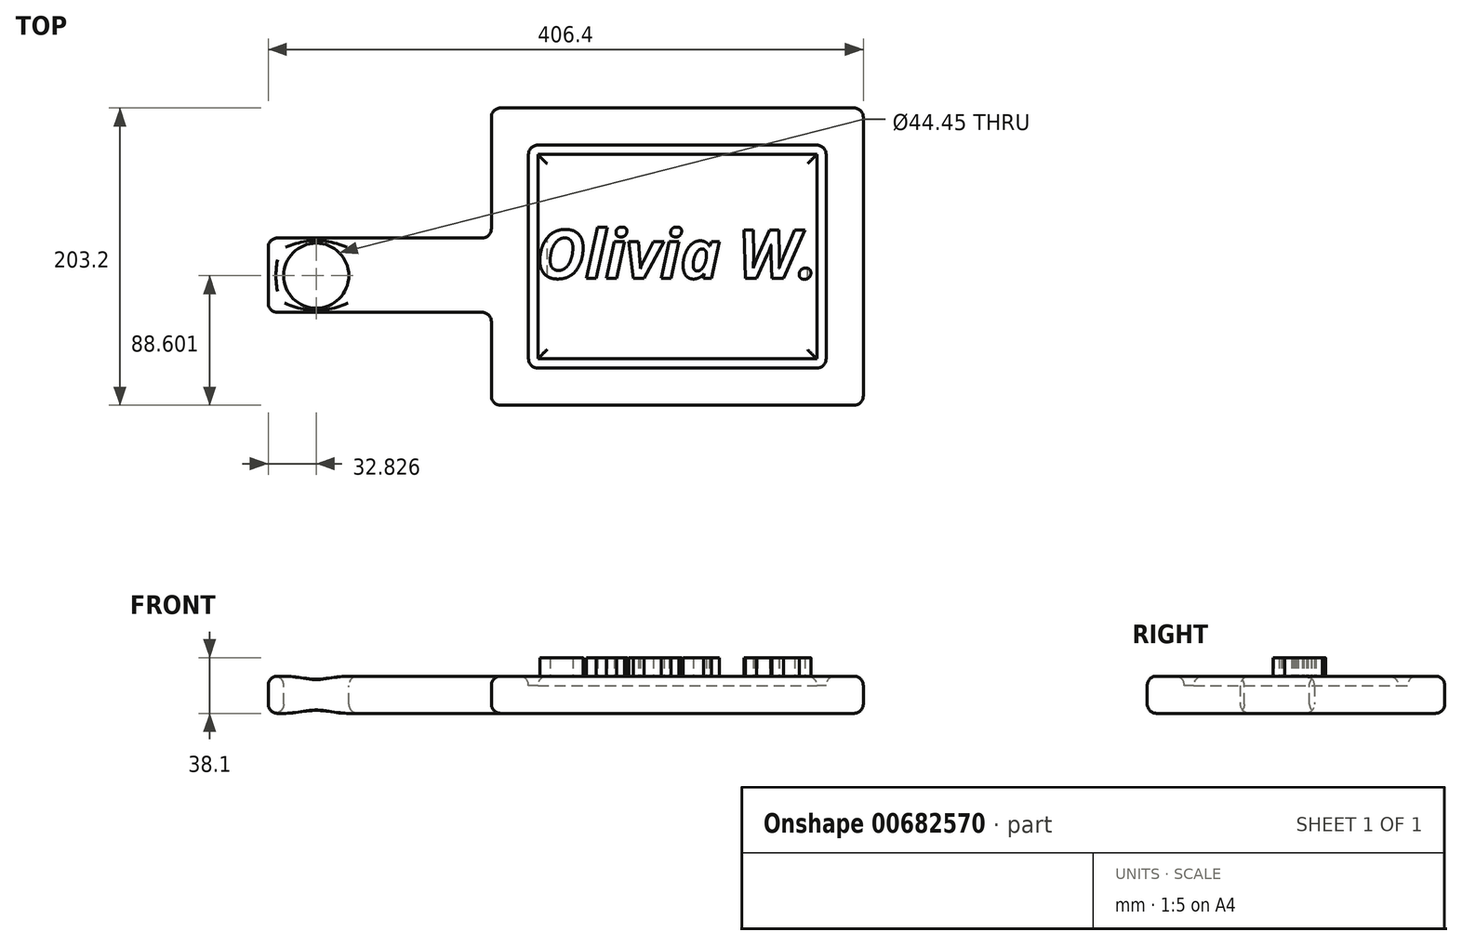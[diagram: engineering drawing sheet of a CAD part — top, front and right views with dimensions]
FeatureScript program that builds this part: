
annotation { "Feature Type Name" : "Feature", "Feature Type Description" : "" }
export const myFeature = defineFeature(function(context is Context, id is Id, definition is map)
    precondition{}
    {
        {
            var Q0;
            Q0=qCreatedBy(makeId("Top.planeOp"),FACE);
            var sketch = newSketch(context, id + "F0", { "sketchPlane" : qUnion([Q0])});
            skLineSegment(sketch, "E0.bottom", {"start": v(0, 0) * mm, "end": v(254, 0) * mm});
            skLineSegment(sketch, "E0.top", {"start": v(0, 203.2) * mm, "end": v(254, 203.2) * mm});
            skLineSegment(sketch, "E0.left", {"start": v(0, 0) * mm, "end": v(0, 203.2) * mm});
            skLineSegment(sketch, "E0.right", {"start": v(254, 0) * mm, "end": v(254, 203.2) * mm});
            skLineSegment(sketch, "E1.bottom", {"start": v(0, 114.3) * mm, "end": v(-152.4, 114.3) * mm});
            skLineSegment(sketch, "E1.top", {"start": v(0, 63.5) * mm, "end": v(-152.4, 63.5) * mm});
            skLineSegment(sketch, "E1.left", {"start": v(0, 114.3) * mm, "end": v(0, 63.5) * mm});
            skLineSegment(sketch, "E1.right", {"start": v(-152.4, 114.3) * mm, "end": v(-152.4, 63.5) * mm});
            skSolve(sketch);
        }
        {
            var Q0;
            {var subQ3=sQuery(id+"F0.wireOp",EDGE,"E0.bottom");Q0=makeQuery(id+"F0.imprint","IMPRINT",FACE,{"disambiguationData":[TD([[makeQuery(id+"F0.imprint","IMPRINT",EDGE,{"derivedFrom":subQ3}),1.0]])]});}
            var sketch = newSketch(context, id + "F1", { "sketchPlane" : qUnion([Q0])});
            skSolve(sketch);
        }
        {
            var Q0;
            Q0 = qSketchRegion(id + "F1", true);
            var Q1;
            {var subQ3=sQuery(id+"F0.wireOp",EDGE,"E0.bottom");Q1=makeQuery(id+"F0.imprint","IMPRINT",FACE,{"disambiguationData":[TD([[makeQuery(id+"F0.imprint","IMPRINT",EDGE,{"derivedFrom":subQ3}),1.0]])]});}
            var Q2;
            Q2=makeQuery(id+"F0.imprint","IMPRINT",FACE,{"disambiguationData":[TD([[makeQuery(id+"F0.imprint","IMPRINT",EDGE,{"derivedFrom":sQuery(id+"F0.wireOp",EDGE,"E1.bottom")}),1.0]])]});
            extrude(context, id + "F2", {"entities" : qUnion([Q0, Q1, Q2]), "depth" : 25.4 * mm, "offsetDistance" : 25.4 * mm});
        }
        {
            var Q0;
            Q0=makeQuery(id+"F2.opExtrude","CAP_FACE",FACE,{"disambiguationData":[OSD([sQuery(id+"F0.wireOp",EDGE,"E0.bottom"),sQuery(id+"F0.wireOp",EDGE,"E0.top"),sQuery(id+"F0.wireOp",EDGE,"E0.left"),sQuery(id+"F0.wireOp",EDGE,"E0.right"),sQuery(id+"F0.wireOp",EDGE,"E1.bottom"),sQuery(id+"F0.wireOp",EDGE,"E1.top"),sQuery(id+"F0.wireOp",EDGE,"E1.right")])],"isStart":false});
            var sketch = newSketch(context, id + "F3", { "sketchPlane" : qUnion([Q0])});
            skCircle(sketch, "E2", {"center": v(-119.57, 88.6) * mm, "radius": 22.23 * mm});
            skSolve(sketch);
        }
        {
            var Q0;
            Q0=makeQuery(id+"F3.imprint","IMPRINT",FACE,{"disambiguationData":[TD([[makeQuery(id+"F3.imprint","IMPRINT",EDGE,{"derivedFrom":sQuery(id+"F3.wireOp",EDGE,"E2")}),1.0]])]});
            extrude(context, id + "F4", {"entities" : qUnion([Q0]), "operationType" : NewBodyOperationType.REMOVE, "oppositeDirection" : true, "depth" : 25.4 * mm, "offsetDistance" : 25.4 * mm});
        }
        {
            var Q0;
            Q0=makeQuery(id+"F2.opExtrude","CAP_FACE",FACE,{"disambiguationData":[OSD([sQuery(id+"F0.wireOp",EDGE,"E0.bottom"),sQuery(id+"F0.wireOp",EDGE,"E0.top"),sQuery(id+"F0.wireOp",EDGE,"E0.left"),sQuery(id+"F0.wireOp",EDGE,"E0.right"),sQuery(id+"F0.wireOp",EDGE,"E1.bottom"),sQuery(id+"F0.wireOp",EDGE,"E1.top"),sQuery(id+"F0.wireOp",EDGE,"E1.right")])],"isStart":false});
            var sketch = newSketch(context, id + "F5", { "sketchPlane" : qUnion([Q0])});
            skLineSegment(sketch, "E3.0", {"start": v(0, 177.8) * mm, "end": v(254, 177.8) * mm});
            skLineSegment(sketch, "E4.0", {"start": v(25.4, 0) * mm, "end": v(25.4, 63.5) * mm});
            skLineSegment(sketch, "E5.0", {"start": v(25.4, 114.3) * mm, "end": v(25.4, 203.2) * mm});
            skLineSegment(sketch, "E6.0", {"start": v(0, 25.4) * mm, "end": v(254, 25.4) * mm});
            skLineSegment(sketch, "E7.0", {"start": v(228.6, 0) * mm, "end": v(228.6, 203.2) * mm});
            skLineSegment(sketch, "E8", {"start": v(25.4, 114.3) * mm, "end": v(25.4, 63.5) * mm});
            skLineSegment(sketch, "E9.0", {"start": v(0, 171.45) * mm, "end": v(254, 171.45) * mm});
            skLineSegment(sketch, "E10.0", {"start": v(31.75, 114.3) * mm, "end": v(31.75, 203.2) * mm});
            skLineSegment(sketch, "E10.1", {"start": v(31.75, 114.3) * mm, "end": v(31.75, 63.5) * mm});
            skLineSegment(sketch, "E10.2", {"start": v(31.75, 0) * mm, "end": v(31.75, 63.5) * mm});
            skLineSegment(sketch, "E11.0", {"start": v(0, 31.75) * mm, "end": v(254, 31.75) * mm});
            skLineSegment(sketch, "E12.0", {"start": v(222.25, 0) * mm, "end": v(222.25, 203.2) * mm});
            skSolve(sketch);
        }
        {
            var Q0;
            {var subQ0=sQuery(id+"F5.wireOp",EDGE,"E5.0");var subQ1=sQuery(id+"F5.wireOp",EDGE,"E3.0");var subQ2=makeQuery(id+"F5.imprint","INTERSECT",VERTEX,{"derivedFrom":[subQ1,subQ0]});Q0=makeQuery(id+"F5.imprint","IMPRINT",FACE,{"disambiguationData":[TD([[makeQuery(id+"F5.imprint","IMPRINT",EDGE,{"disambiguationData":[TD([[subQ2,-1.0]])],"derivedFrom":subQ1}),-1.0]])]});}
            var Q1;
            {var subQ0=sQuery(id+"F5.wireOp",EDGE,"E10.0");var subQ1=sQuery(id+"F5.wireOp",EDGE,"E3.0");var subQ2=makeQuery(id+"F5.imprint","INTERSECT",VERTEX,{"derivedFrom":[subQ1,subQ0]});Q1=makeQuery(id+"F5.imprint","IMPRINT",FACE,{"disambiguationData":[TD([[makeQuery(id+"F5.imprint","IMPRINT",EDGE,{"disambiguationData":[TD([[subQ2,-1.0]])],"derivedFrom":subQ1}),-1.0]])]});}
            var Q2;
            {var subQ0=sQuery(id+"F5.wireOp",EDGE,"E12.0");var subQ1=sQuery(id+"F5.wireOp",EDGE,"E3.0");var subQ2=makeQuery(id+"F5.imprint","INTERSECT",VERTEX,{"derivedFrom":[subQ1,subQ0]});Q2=makeQuery(id+"F5.imprint","IMPRINT",FACE,{"disambiguationData":[TD([[makeQuery(id+"F5.imprint","IMPRINT",EDGE,{"disambiguationData":[TD([[subQ2,-1.0]])],"derivedFrom":subQ1}),-1.0]])]});}
            var Q3;
            {var subQ0=sQuery(id+"F5.wireOp",EDGE,"E6.0");var subQ1=sQuery(id+"F5.wireOp",EDGE,"E4.0");var subQ2=makeQuery(id+"F5.imprint","INTERSECT",VERTEX,{"derivedFrom":[subQ1,subQ0]});Q3=makeQuery(id+"F5.imprint","IMPRINT",FACE,{"disambiguationData":[TD([[makeQuery(id+"F5.imprint","IMPRINT",EDGE,{"disambiguationData":[TD([[subQ2,-1.0]])],"derivedFrom":subQ1}),-1.0]])]});}
            var Q4;
            {var subQ0=sQuery(id+"F5.wireOp",EDGE,"E10.2");var subQ1=sQuery(id+"F5.wireOp",EDGE,"E6.0");var subQ2=makeQuery(id+"F5.imprint","INTERSECT",VERTEX,{"derivedFrom":[subQ1,subQ0]});Q4=makeQuery(id+"F5.imprint","IMPRINT",FACE,{"disambiguationData":[TD([[makeQuery(id+"F5.imprint","IMPRINT",EDGE,{"disambiguationData":[TD([[subQ2,-1.0]])],"derivedFrom":subQ1}),1.0]])]});}
            var Q5;
            {var subQ0=sQuery(id+"F5.wireOp",EDGE,"E12.0");var subQ1=sQuery(id+"F5.wireOp",EDGE,"E6.0");var subQ2=makeQuery(id+"F5.imprint","INTERSECT",VERTEX,{"derivedFrom":[subQ1,subQ0]});Q5=makeQuery(id+"F5.imprint","IMPRINT",FACE,{"disambiguationData":[TD([[makeQuery(id+"F5.imprint","IMPRINT",EDGE,{"disambiguationData":[TD([[subQ2,-1.0]])],"derivedFrom":subQ1}),1.0]])]});}
            var Q6;
            {var subQ0=sQuery(id+"F5.wireOp",EDGE,"E11.0");var subQ1=sQuery(id+"F5.wireOp",EDGE,"E7.0");var subQ2=makeQuery(id+"F5.imprint","INTERSECT",VERTEX,{"derivedFrom":[subQ1,subQ0]});Q6=makeQuery(id+"F5.imprint","IMPRINT",FACE,{"disambiguationData":[TD([[makeQuery(id+"F5.imprint","IMPRINT",EDGE,{"disambiguationData":[TD([[subQ2,-1.0]])],"derivedFrom":subQ1}),1.0]])]});}
            var Q7;
            {var subQ0=sQuery(id+"F5.wireOp",EDGE,"E8");Q7=makeQuery(id+"F5.imprint","IMPRINT",FACE,{"disambiguationData":[TD([[makeQuery(id+"F5.imprint","IMPRINT",EDGE,{"derivedFrom":subQ0}),1.0]])]});}
            extrude(context, id + "F6", {"entities" : qUnion([Q0, Q1, Q2, Q3, Q4, Q5, Q6, Q7]), "operationType" : NewBodyOperationType.REMOVE, "oppositeDirection" : true, "depth" : 6.35 * mm, "offsetDistance" : 25.4 * mm});
        }
        {
            var Q0;
            Q0=makeQuery(id+"F2.opExtrude","SWEPT_EDGE",EDGE,{"disambiguationData":[OSD([sQuery(id+"F0.wireOp",EDGE,"E0.top"),sQuery(id+"F0.wireOp",EDGE,"E0.left")])]});
            var Q1;
            Q1=makeQuery(id+"F2.opExtrude","SWEPT_EDGE",EDGE,{"disambiguationData":[OSD([sQuery(id+"F0.wireOp",EDGE,"E0.left"),sQuery(id+"F0.wireOp",EDGE,"E1.bottom"),sQuery(id+"F0.wireOp",EDGE,"E1.left")])]});
            var Q2;
            Q2=makeQuery(id+"F2.opExtrude","SWEPT_EDGE",EDGE,{"disambiguationData":[OSD([sQuery(id+"F0.wireOp",EDGE,"E1.bottom"),sQuery(id+"F0.wireOp",EDGE,"E1.right")])]});
            var Q3;
            Q3=makeQuery(id+"F2.opExtrude","SWEPT_EDGE",EDGE,{"disambiguationData":[OSD([sQuery(id+"F0.wireOp",EDGE,"E1.top"),sQuery(id+"F0.wireOp",EDGE,"E1.right")])]});
            var Q4;
            Q4=makeQuery(id+"F2.opExtrude","SWEPT_EDGE",EDGE,{"disambiguationData":[OSD([sQuery(id+"F0.wireOp",EDGE,"E0.bottom"),sQuery(id+"F0.wireOp",EDGE,"E0.left")])]});
            var Q5;
            Q5=makeQuery(id+"F2.opExtrude","SWEPT_EDGE",EDGE,{"disambiguationData":[OSD([sQuery(id+"F0.wireOp",EDGE,"E0.top"),sQuery(id+"F0.wireOp",EDGE,"E0.right")])]});
            var Q6;
            Q6=makeQuery(id+"F2.opExtrude","SWEPT_EDGE",EDGE,{"disambiguationData":[OSD([sQuery(id+"F0.wireOp",EDGE,"E0.bottom"),sQuery(id+"F0.wireOp",EDGE,"E0.right")])]});
            var Q7;
            Q7=makeQuery(id+"F6.boolean.opBoolean","COPY",EDGE,{"derivedFrom":makeQuery(id+"F6.opExtrude","SWEPT_EDGE",EDGE,{"disambiguationData":[OSD([sQuery(id+"F5.wireOp",EDGE,"E3.0"),sQuery(id+"F5.wireOp",EDGE,"E5.0")])]})});
            var Q8;
            Q8=makeQuery(id+"F6.boolean.opBoolean","COPY",EDGE,{"derivedFrom":makeQuery(id+"F6.opExtrude","SWEPT_EDGE",EDGE,{"disambiguationData":[OSD([sQuery(id+"F5.wireOp",EDGE,"E4.0"),sQuery(id+"F5.wireOp",EDGE,"E6.0")])]})});
            var Q9;
            Q9=makeQuery(id+"F6.boolean.opBoolean","COPY",EDGE,{"derivedFrom":makeQuery(id+"F6.opExtrude","SWEPT_EDGE",EDGE,{"disambiguationData":[OSD([sQuery(id+"F5.wireOp",EDGE,"E6.0"),sQuery(id+"F5.wireOp",EDGE,"E7.0")])]})});
            var Q10;
            Q10=makeQuery(id+"F6.boolean.opBoolean","COPY",EDGE,{"derivedFrom":makeQuery(id+"F6.opExtrude","SWEPT_EDGE",EDGE,{"disambiguationData":[OSD([sQuery(id+"F5.wireOp",EDGE,"E3.0"),sQuery(id+"F5.wireOp",EDGE,"E7.0")])]})});
            var Q11;
            Q11=makeQuery(id+"F2.opExtrude","SWEPT_EDGE",EDGE,{"disambiguationData":[OSD([sQuery(id+"F0.wireOp",EDGE,"E0.left"),sQuery(id+"F0.wireOp",EDGE,"E1.top"),sQuery(id+"F0.wireOp",EDGE,"E1.left")])]});
            var Q12;
            Q12=makeQuery(id+"F6.boolean.opBoolean","SPLIT",FACE,{"disambiguationData":[TD([makeQuery(id+"F6.opExtrude","SWEPT_FACE",FACE,{"disambiguationData":[OSD([sQuery(id+"F5.wireOp",EDGE,"E9.0")])]})])],"derivedFrom":makeQuery(id+"F2.opExtrude","CAP_FACE",FACE,{"disambiguationData":[OSD([sQuery(id+"F0.wireOp",EDGE,"E0.bottom"),sQuery(id+"F0.wireOp",EDGE,"E0.top"),sQuery(id+"F0.wireOp",EDGE,"E0.left"),sQuery(id+"F0.wireOp",EDGE,"E0.right"),sQuery(id+"F0.wireOp",EDGE,"E1.bottom"),sQuery(id+"F0.wireOp",EDGE,"E1.top"),sQuery(id+"F0.wireOp",EDGE,"E1.right")])],"isStart":false})});
            var Q13;
            {var subQ0=sQuery(id+"F0.wireOp",EDGE,"E1.right");var subQ1=sQuery(id+"F0.wireOp",EDGE,"E1.top");var subQ2=sQuery(id+"F0.wireOp",EDGE,"E1.bottom");var subQ3=sQuery(id+"F0.wireOp",EDGE,"E0.right");var subQ4=sQuery(id+"F0.wireOp",EDGE,"E0.bottom");var subQ5=sQuery(id+"F0.wireOp",EDGE,"E0.left");var subQ6=sQuery(id+"F0.wireOp",EDGE,"E0.top");Q13=makeQuery(id+"F6.boolean.opBoolean","SPLIT",FACE,{"disambiguationData":[TD([makeQuery(id+"F2.opExtrude","SWEPT_FACE",FACE,{"disambiguationData":[OSD([subQ4])]})])],"derivedFrom":makeQuery(id+"F2.opExtrude","CAP_FACE",FACE,{"disambiguationData":[OSD([subQ4,subQ6,subQ5,subQ3,subQ2,subQ1,subQ0])],"isStart":false})});}
            var Q14;
            Q14=makeQuery(id+"F2.opExtrude","CAP_FACE",FACE,{"disambiguationData":[OSD([sQuery(id+"F0.wireOp",EDGE,"E0.bottom"),sQuery(id+"F0.wireOp",EDGE,"E0.top"),sQuery(id+"F0.wireOp",EDGE,"E0.left"),sQuery(id+"F0.wireOp",EDGE,"E0.right"),sQuery(id+"F0.wireOp",EDGE,"E1.bottom"),sQuery(id+"F0.wireOp",EDGE,"E1.top"),sQuery(id+"F0.wireOp",EDGE,"E1.right")])],"isStart":true});
            fillet(context, id + "F7", {"entities" : qUnion([Q0, Q1, Q2, Q3, Q4, Q5, Q6, Q7, Q8, Q9, Q10, Q11, Q12, Q13, Q14]), "radius" : 6.35 * mm, "tangentPropagation" : true, "allowEdgeOverflow" : false});
        }
        {
            var Q0;
            Q0=makeQuery(id+"F6.boolean.opBoolean","SPLIT",FACE,{"disambiguationData":[TD([makeQuery(id+"F6.opExtrude","SWEPT_FACE",FACE,{"disambiguationData":[OSD([sQuery(id+"F5.wireOp",EDGE,"E9.0")])]})])],"derivedFrom":makeQuery(id+"F2.opExtrude","CAP_FACE",FACE,{"disambiguationData":[OSD([sQuery(id+"F0.wireOp",EDGE,"E0.bottom"),sQuery(id+"F0.wireOp",EDGE,"E0.top"),sQuery(id+"F0.wireOp",EDGE,"E0.left"),sQuery(id+"F0.wireOp",EDGE,"E0.right"),sQuery(id+"F0.wireOp",EDGE,"E1.bottom"),sQuery(id+"F0.wireOp",EDGE,"E1.top"),sQuery(id+"F0.wireOp",EDGE,"E1.right")])],"isStart":false})});
            var sketch = newSketch(context, id + "F8", { "sketchPlane" : qUnion([Q0])});
            skText(sketch, "E13", { "text": "Olivia W.", "fontName": "OpenSans-BoldItalic.ttf"});
            const initialGuessF8  = {"E13": [0.0304, 0.08672, 1, 0, 0.03326]};
            skSetInitialGuess(sketch, initialGuessF8);
            skSolve(sketch);
        }
        {
            var Q0;
            Q0 = qSketchRegion(id + "F8", true);
            extrude(context, id + "F9", {"entities" : qUnion([Q0]), "operationType" : NewBodyOperationType.ADD, "depth" : 12.7 * mm, "offsetDistance" : 25.4 * mm});
        }
    });
